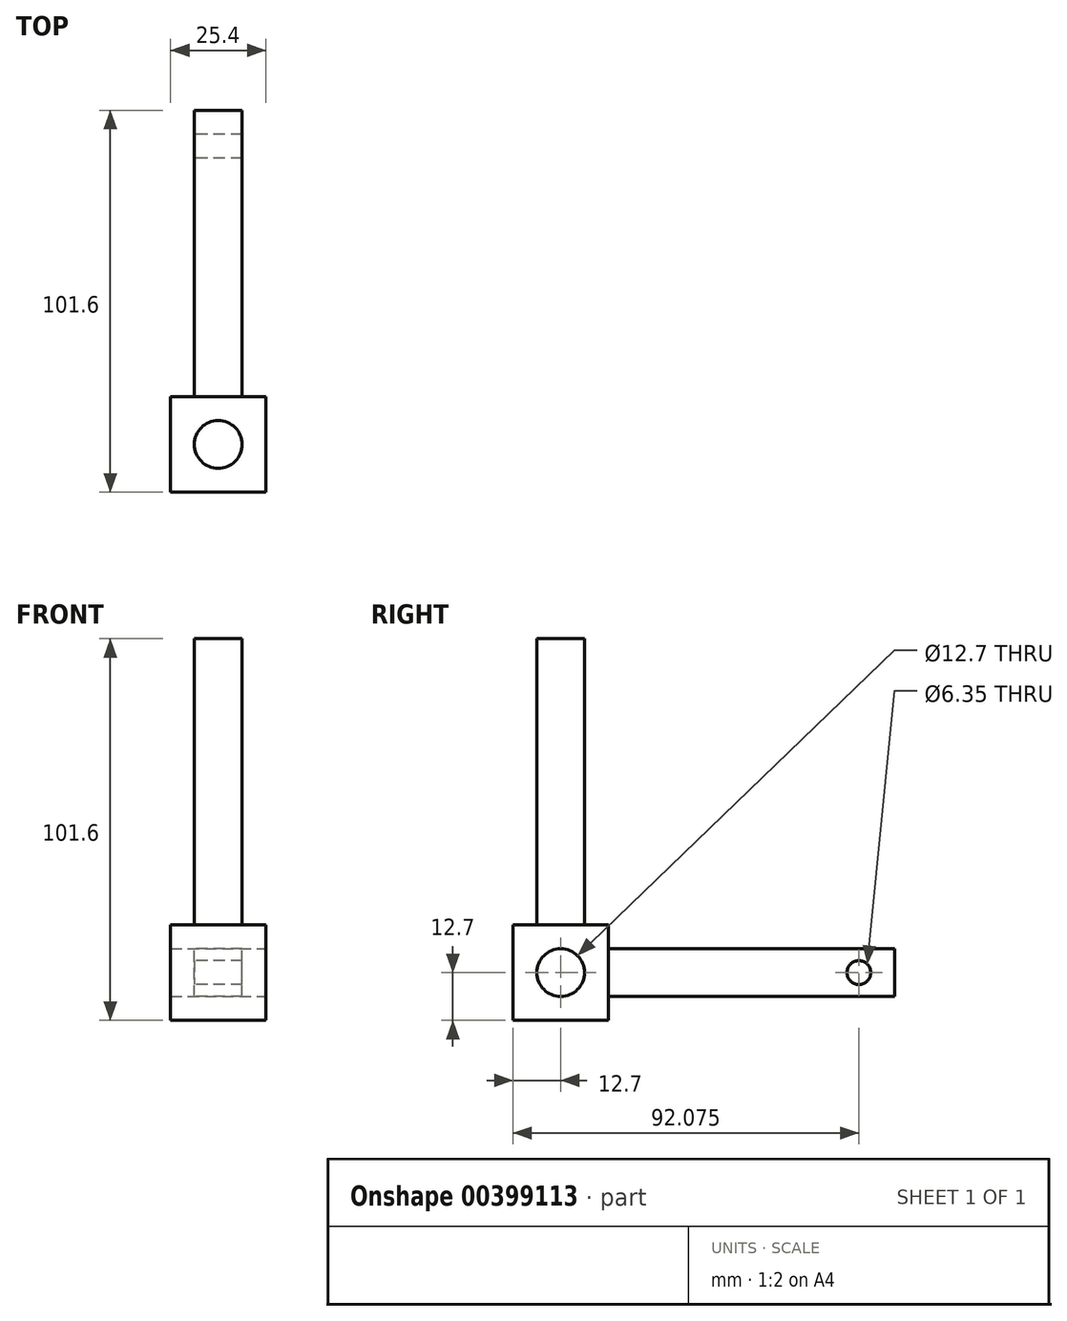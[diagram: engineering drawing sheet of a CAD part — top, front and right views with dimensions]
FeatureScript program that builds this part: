
annotation { "Feature Type Name" : "Feature", "Feature Type Description" : "" }
export const myFeature = defineFeature(function(context is Context, id is Id, definition is map)
    precondition{}
    {
        {
            var Q0;
            Q0=qCreatedBy(makeId("Right.planeOp"),FACE);
            var sketch = newSketch(context, id + "F0", { "sketchPlane" : qUnion([Q0])});
            skLineSegment(sketch, "E0.bottom", {"start": v(-12.7, -12.7) * mm, "end": v(12.7, -12.7) * mm});
            skLineSegment(sketch, "E0.top", {"start": v(-12.7, 12.7) * mm, "end": v(12.7, 12.7) * mm});
            skLineSegment(sketch, "E0.left", {"start": v(-12.7, -12.7) * mm, "end": v(-12.7, 12.7) * mm});
            skLineSegment(sketch, "E0.right", {"start": v(12.7, -12.7) * mm, "end": v(12.7, 12.7) * mm});
            skPoint(sketch, "E0.middle", {"position": v(0, 0) * mm});
            skSolve(sketch);
        }
        {
            var Q0;
            Q0=makeQuery(id+"F0.imprint","IMPRINT",FACE,{"disambiguationData":[TD([[makeQuery(id+"F0.imprint","IMPRINT",EDGE,{"derivedFrom":sQuery(id+"F0.wireOp",EDGE,"E0.bottom")}),1.0]])]});
            extrude(context, id + "F1", {"entities" : qUnion([Q0]), "depth" : 25.4 * mm});
        }
        {
            var Q0;
            Q0=makeQuery(id+"F1.opExtrude","CAP_FACE",FACE,{"disambiguationData":[OSD([sQuery(id+"F0.wireOp",EDGE,"E0.bottom"),sQuery(id+"F0.wireOp",EDGE,"E0.top"),sQuery(id+"F0.wireOp",EDGE,"E0.left"),sQuery(id+"F0.wireOp",EDGE,"E0.right")])],"isStart":false});
            var sketch = newSketch(context, id + "F2", { "sketchPlane" : qUnion([Q0])});
            skCircle(sketch, "E1", {"center": v(0, 0) * mm, "radius": 6.35 * mm});
            skSolve(sketch);
        }
        {
            var Q0;
            Q0=makeQuery(id+"F2.imprint","IMPRINT",FACE,{"disambiguationData":[TD([[makeQuery(id+"F2.imprint","IMPRINT",EDGE,{"derivedFrom":sQuery(id+"F2.wireOp",EDGE,"E1")}),1.0]])]});
            extrude(context, id + "F3", {"entities" : qUnion([Q0]), "operationType" : NewBodyOperationType.REMOVE, "oppositeDirection" : true, "depth" : 25.4 * mm});
        }
        {
            var Q0;
            Q0=makeQuery(id+"F1.opExtrude","SWEPT_FACE",FACE,{"disambiguationData":[OSD([sQuery(id+"F0.wireOp",EDGE,"E0.top")])]});
            var sketch = newSketch(context, id + "F4", { "sketchPlane" : qUnion([Q0])});
            skCircle(sketch, "E2", {"center": v(12.7, 0) * mm, "radius": 6.35 * mm});
            skSolve(sketch);
        }
        {
            var Q0;
            Q0=makeQuery(id+"F4.imprint","IMPRINT",FACE,{"disambiguationData":[TD([[makeQuery(id+"F4.imprint","IMPRINT",EDGE,{"derivedFrom":sQuery(id+"F4.wireOp",EDGE,"E2")}),1.0]])]});
            extrude(context, id + "F5", {"entities" : qUnion([Q0]), "operationType" : NewBodyOperationType.ADD, "depth" : 76.2 * mm});
        }
        {
            var Q0;
            Q0=makeQuery(id+"F1.opExtrude","SWEPT_FACE",FACE,{"disambiguationData":[OSD([sQuery(id+"F0.wireOp",EDGE,"E0.right")])]});
            var sketch = newSketch(context, id + "F6", { "sketchPlane" : qUnion([Q0])});
            skLineSegment(sketch, "E3.bottom", {"start": v(-19.05, -6.35) * mm, "end": v(-6.35, -6.35) * mm});
            skLineSegment(sketch, "E3.top", {"start": v(-19.05, 6.35) * mm, "end": v(-6.35, 6.35) * mm});
            skLineSegment(sketch, "E3.left", {"start": v(-19.05, -6.35) * mm, "end": v(-19.05, 6.35) * mm});
            skLineSegment(sketch, "E3.right", {"start": v(-6.35, -6.35) * mm, "end": v(-6.35, 6.35) * mm});
            skPoint(sketch, "E3.middle", {"position": v(-12.7, 0) * mm});
            skSolve(sketch);
        }
        {
            var Q0;
            Q0=makeQuery(id+"F6.imprint","IMPRINT",FACE,{"disambiguationData":[TD([[makeQuery(id+"F6.imprint","IMPRINT",EDGE,{"derivedFrom":sQuery(id+"F6.wireOp",EDGE,"E3.bottom")}),1.0]])]});
            extrude(context, id + "F7", {"entities" : qUnion([Q0]), "operationType" : NewBodyOperationType.ADD, "depth" : 76.2 * mm});
        }
        {
            var Q0;
            Q0=makeQuery(id+"F7.opExtrude","SWEPT_FACE",FACE,{"disambiguationData":[OSD([sQuery(id+"F6.wireOp",EDGE,"E3.right")])]});
            var sketch = newSketch(context, id + "F8", { "sketchPlane" : qUnion([Q0])});
            skCircle(sketch, "E4", {"center": v(-79.38, 0) * mm, "radius": 3.18 * mm});
            skSolve(sketch);
        }
        {
            var Q0;
            Q0=makeQuery(id+"F8.imprint","IMPRINT",FACE,{"disambiguationData":[TD([[makeQuery(id+"F8.imprint","IMPRINT",EDGE,{"derivedFrom":sQuery(id+"F8.wireOp",EDGE,"E4")}),1.0]])]});
            extrude(context, id + "F9", {"entities" : qUnion([Q0]), "operationType" : NewBodyOperationType.REMOVE, "oppositeDirection" : true, "depth" : 25.4 * mm});
        }
    });
